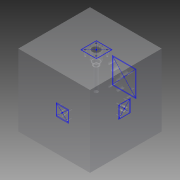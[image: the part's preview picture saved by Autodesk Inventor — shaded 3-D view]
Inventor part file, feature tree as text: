
AUTODESK INVENTOR PART (.ipt)
format: ipt  version: 2014 (Build 180170000, 170)  size: 455,168 bytes
history: native  units: mm
features: other x52, sketch x5, extrude x1
ambient origin geometry x8: Origin, YZ Plane, XZ Plane, XY Plane, X Axis, Y Axis, Z Axis, Center Point
bodies: 实体1 (feature_tree)
feature tree (58):
  extrude  "拉伸1"  TaperAngle=0.0deg  [1 undecoded]
  other  "UCS1"
  other  "UCS2"
  other  "UCS3"
  other  "UCS4"
  other  "UCS5"
  other  "UCS6"
  other  "Footprint1"
  other  "Footprint2"
  other  "Footprint3"
  other  "Footprint4"
  sketch  "草图1"  dims[d0=300.0mm d1=0.0mm]
  other  "UCS1: YZ 平面"
  other  "UCS1: XZ 平面"
  other  "UCS1: XY 平面"
  other  "UCS1: X 轴"
  other  "UCS1: Y 轴"
  other  "UCS1: Z 轴"
  other  "UCS1: 原点"
  other  "UCS2: YZ 平面"
  other  "UCS2: XZ 平面"
  other  "UCS2: XY 平面"
  other  "UCS2: X 轴"
  other  "UCS2: Y 轴"
  other  "UCS2: Z 轴"
  other  "UCS2: 原点"
  other  "UCS3: YZ 平面"
  other  "UCS3: XZ 平面"
  other  "UCS3: XY 平面"
  other  "UCS3: X 轴"
  other  "UCS3: Y 轴"
  other  "UCS3: Z 轴"
  other  "UCS3: 原点"
  other  "UCS4: YZ 平面"
  other  "UCS4: XZ 平面"
  other  "UCS4: XY 平面"
  other  "UCS4: X 轴"
  other  "UCS4: Y 轴"
  other  "UCS4: Z 轴"
  other  "UCS4: 原点"
  other  "UCS5: YZ 平面"
  other  "UCS5: XZ 平面"
  other  "UCS5: XY 平面"
  other  "UCS5: X 轴"
  other  "UCS5: Y 轴"
  other  "UCS5: Z 轴"
  other  "UCS5: 原点"
  other  "UCS6: YZ 平面"
  other  "UCS6: XZ 平面"
  other  "UCS6: XY 平面"
  other  "UCS6: X 轴"
  other  "UCS6: Y 轴"
  other  "UCS6: Z 轴"
  other  "UCS6: 原点"
  sketch  "草图2"  dims[d2=0.0mm d3=0.0mm d4=0.0mm d5=0.0mm d6=0.0mm d7=0.0mm]
  sketch  "草图6"  dims[d14=0.0mm d15=0.0mm d16=0.0mm d17=0.0mm d18=0.0mm d19=0.0mm]
  sketch  "草图8"  dims[d20=0.0mm d21=0.0mm d22=0.0mm d23=0.0mm d24=0.0mm d25=0.0mm d26=0.0mm d27=0.0mm d28=0.0mm d29=0.0mm d30=0.0mm d31=0.0mm d32=0.0mm d33=0.0mm d34=0.0mm d35=0.0mm d36=0.0mm d37=0.0mm d38=0.0mm d44=0.0mm d58=0.0mm d72=0.0mm d73=0.0mm]
  sketch  "草图4"  dims[d8=0.0mm d9=0.0mm d10=0.0mm d11=0.0mm d12=0.0mm d13=0.0mm]
note: 1 required parameter value undecoded (feature->parameter linkage not recoverable at this tier; creation-order binding heuristic only, values carry confidence <= 0.55)
